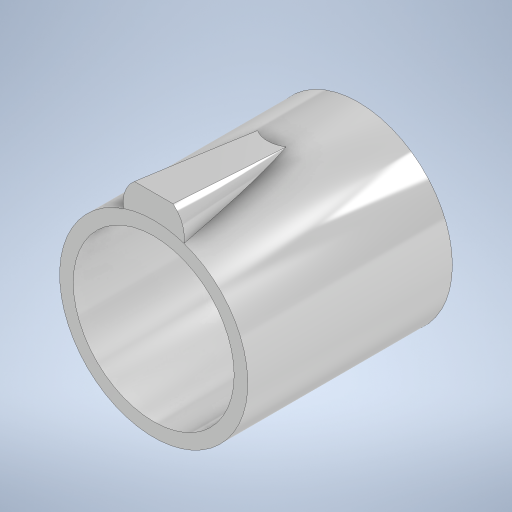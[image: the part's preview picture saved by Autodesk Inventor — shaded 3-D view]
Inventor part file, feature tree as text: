
AUTODESK INVENTOR PART (.ipt)
format: ipt  version: 2023 (Build 270158000, 158)  size: 260,608 bytes
history: native  units: mm
features: extrude x2, other x1, sketch x1
ambient origin geometry x8: Origin, YZ Plane, XZ Plane, XY Plane, X Axis, Y Axis, Z Axis, Center Point
bodies: Body1 (feature_tree)
feature tree (4):
  other  "Твердое тело1"
  sketch  "Эскиз1"
  extrude  "Выдавливание1"  Depth=118.0mm
  extrude  "Выдавливание2"  Depth=138.0mm
